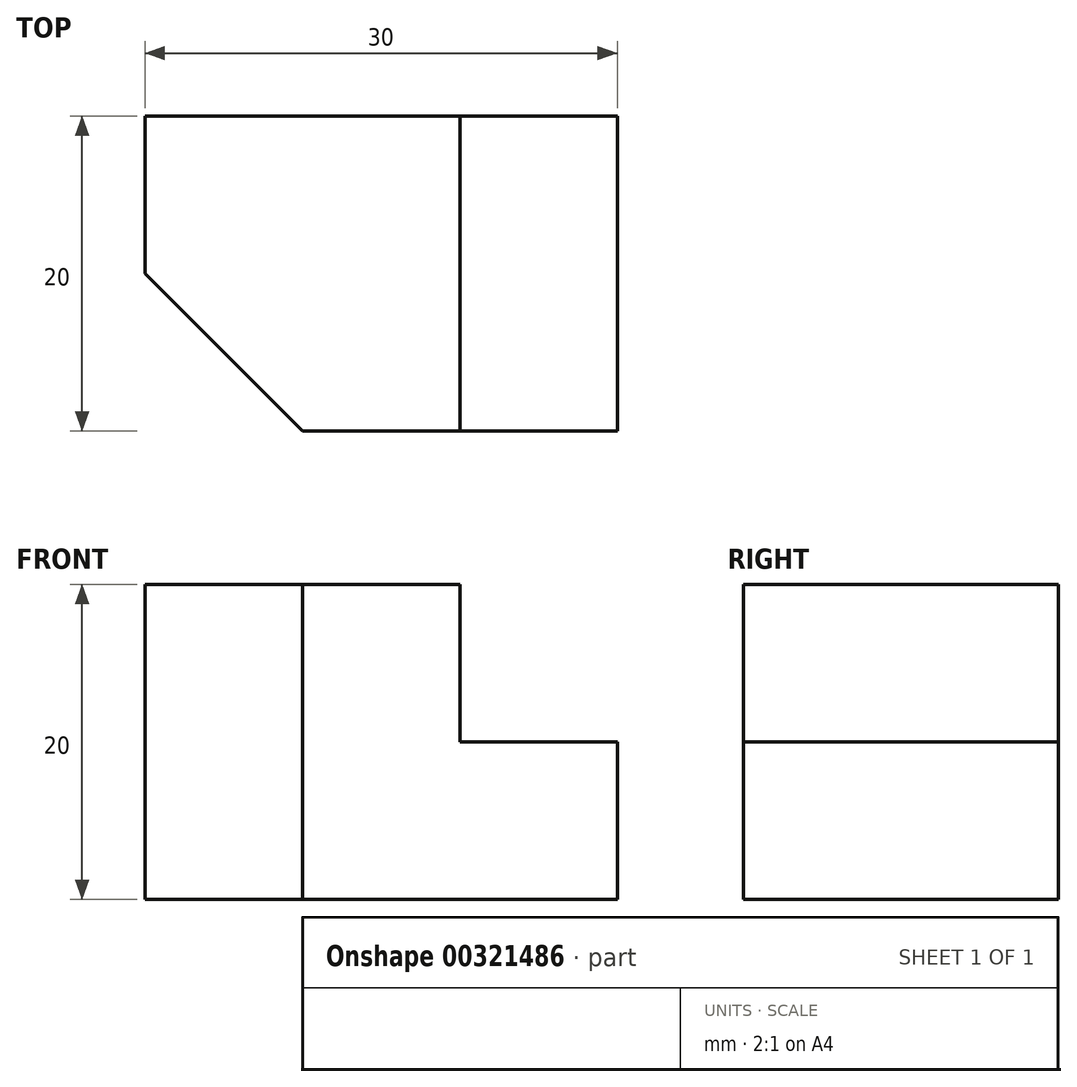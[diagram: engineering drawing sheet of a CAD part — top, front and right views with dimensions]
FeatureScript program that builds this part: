
annotation { "Feature Type Name" : "Feature", "Feature Type Description" : "" }
export const myFeature = defineFeature(function(context is Context, id is Id, definition is map)
    precondition{}
    {
        {
            var Q0;
            Q0=qCreatedBy(makeId("Top.planeOp"),FACE);
            var sketch = newSketch(context, id + "F0", { "sketchPlane" : qUnion([Q0])});
            skLineSegment(sketch, "E0", {"start": v(0, 0) * mm, "end": v(20, 0) * mm});
            skLineSegment(sketch, "E1", {"start": v(20, 0) * mm, "end": v(20, 20) * mm});
            skLineSegment(sketch, "E2", {"start": v(20, 20) * mm, "end": v(-10, 20) * mm});
            skLineSegment(sketch, "E3", {"start": v(-10, 20) * mm, "end": v(-10, 10) * mm});
            skLineSegment(sketch, "E4", {"start": v(10, 20) * mm, "end": v(10, 0) * mm});
            skLineSegment(sketch, "E5", {"start": v(-10, 10) * mm, "end": v(0, 0) * mm});
            skSolve(sketch);
        }
        {
            var Q0;
            Q0 = qSketchRegion(id + "F0", true);
            extrude(context, id + "F1", {"entities" : qUnion([Q0]), "depth" : 20 * mm});
        }
        {
            var Q0;
            Q0=makeQuery(id+"F1.opExtrude","CAP_FACE",FACE,{"disambiguationData":[OSD([sQuery(id+"F0.wireOp",EDGE,"E0"),sQuery(id+"F0.wireOp",EDGE,"E1"),sQuery(id+"F0.wireOp",EDGE,"E2"),sQuery(id+"F0.wireOp",EDGE,"E3"),sQuery(id+"F0.wireOp",EDGE,"E5")])],"isStart":false});
            var sketch = newSketch(context, id + "F2", { "sketchPlane" : qUnion([Q0])});
            skLineSegment(sketch, "E6", {"start": v(20, 20) * mm, "end": v(10, 20) * mm});
            skLineSegment(sketch, "E7", {"start": v(10, 20) * mm, "end": v(10, 0) * mm});
            skLineSegment(sketch, "E8", {"start": v(10, 0) * mm, "end": v(20, 0) * mm});
            skLineSegment(sketch, "E9", {"start": v(20, 0) * mm, "end": v(20, 20) * mm});
            skSolve(sketch);
        }
        {
            var Q0;
            Q0=makeQuery(id+"F2.imprint","IMPRINT",FACE,{"disambiguationData":[TD([[makeQuery(id+"F2.imprint","IMPRINT",EDGE,{"derivedFrom":sQuery(id+"F2.wireOp",EDGE,"E6")}),1.0]])]});
            extrude(context, id + "F3", {"entities" : qUnion([Q0]), "operationType" : NewBodyOperationType.REMOVE, "oppositeDirection" : true, "depth" : 10 * mm});
        }
    });
